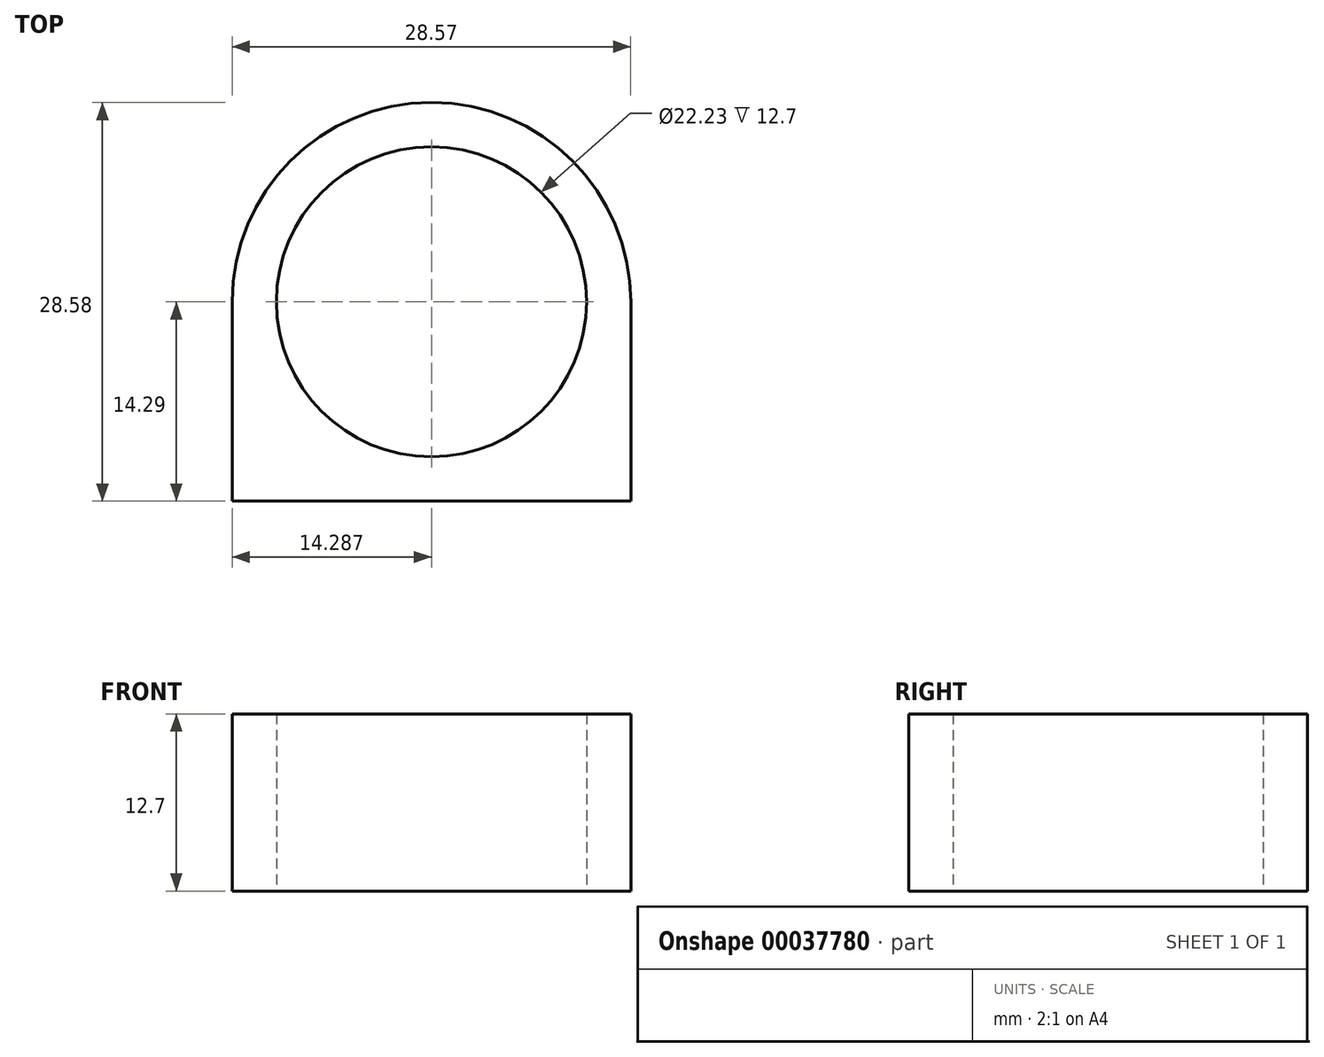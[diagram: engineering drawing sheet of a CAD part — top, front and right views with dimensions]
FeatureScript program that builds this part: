
annotation { "Feature Type Name" : "Feature", "Feature Type Description" : "" }
export const myFeature = defineFeature(function(context is Context, id is Id, definition is map)
    precondition{}
    {
        {
            var Q0;
            Q0=qCreatedBy(makeId("Top.planeOp"),FACE);
            var sketch = newSketch(context, id + "F0", { "sketchPlane" : qUnion([Q0])});
            skLineSegment(sketch, "E0.bottom", {"start": v(0, 0) * mm, "end": v(28.58, 0) * mm, "construction": true});
            skLineSegment(sketch, "E0.top", {"start": v(0, -14.29) * mm, "end": v(28.58, -14.29) * mm});
            skLineSegment(sketch, "E0.left", {"start": v(0, 0) * mm, "end": v(0, -14.29) * mm});
            skLineSegment(sketch, "E0.right", {"start": v(28.58, 0) * mm, "end": v(28.58, -14.29) * mm});
            skCircle(sketch, "E1", {"center": v(14.29, 0) * mm, "radius": 11.11 * mm});
            skArc(sketch, "E2", {"start": v(28.58, 0) * mm, "mid": v(14.29, 14.29) * mm, "end": v(0, 0) * mm});
            skArc(sketch, "E3", {"start": v(0, 0) * mm, "mid": v(14.29, -14.29) * mm, "end": v(28.58, 0) * mm, "construction": true});
            skSolve(sketch);
        }
        {
            var Q0;
            Q0 = qSketchRegion(id + "F0", true);
            extrude(context, id + "F1", {"entities" : qUnion([Q0]), "depth" : 12.7 * mm});
        }
    });
